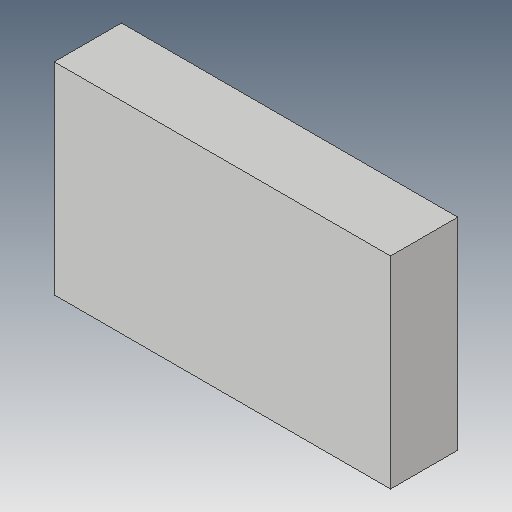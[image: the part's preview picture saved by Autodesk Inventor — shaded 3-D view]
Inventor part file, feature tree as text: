
AUTODESK INVENTOR PART (.ipt)
format: ipt  version: 2018 (Build 220112000, 112)  size: 83,968 bytes
history: native  units: in
note: dims shown in document units (in); Inventor stores cm internally (conversion verified against a paired STEP export)
features: other x3, sketch x1
ambient origin geometry x8: Origin, YZ Plane, XZ Plane, XY Plane, X Axis, Y Axis, Z Axis, Center Point
bodies: Solid1 (feature_tree)
feature tree (4):
  other  "Outrigger.ipt"
  other  "Solid1::Outrigger.ipt"
  other  "TaggingFeature1"
  sketch  "Sketch1"  dims[d0=0.3937in]
